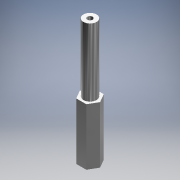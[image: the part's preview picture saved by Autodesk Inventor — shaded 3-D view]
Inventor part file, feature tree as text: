
AUTODESK INVENTOR PART (.ipt)
format: ipt  version: 2017 SP1 (Build 210196100, 196)  size: 116,224 bytes
history: native  units: in
note: dims shown in document units (in); Inventor stores cm internally (conversion verified against a paired STEP export)
features: extrude x4, sketch x4
ambient origin geometry x8: Origin, YZ Plane, XZ Plane, XY Plane, X Axis, Y Axis, Z Axis, Center Point
bodies: Solid1 (feature_tree)
feature tree (8):
  extrude  "Extrusion1"  Depth=1.625in TaperAngle=0.0deg
  extrude  "Extrusion2"  Depth=1.9375in TaperAngle=0.0deg
  extrude  "Extrusion3"  Depth=1.0in TaperAngle=0.0deg
  extrude  "Extrusion4"  [1 undecoded]
  sketch  "Sketch1"  dims[d0=0.5in d1=1.625in d2=0.0in]
  sketch  "Sketch2"  dims[d3=0.375in d4=1.9375in d5=0.0in]
  sketch  "Sketch3"  dims[d7=0.15in d8=1.0in d9=0.0in]
  sketch  "Sketch4"  dims[d10=1.0in d11=0.0in]
note: 1 required parameter value undecoded (feature->parameter linkage not recoverable at this tier; creation-order binding heuristic only, values carry confidence <= 0.55)
